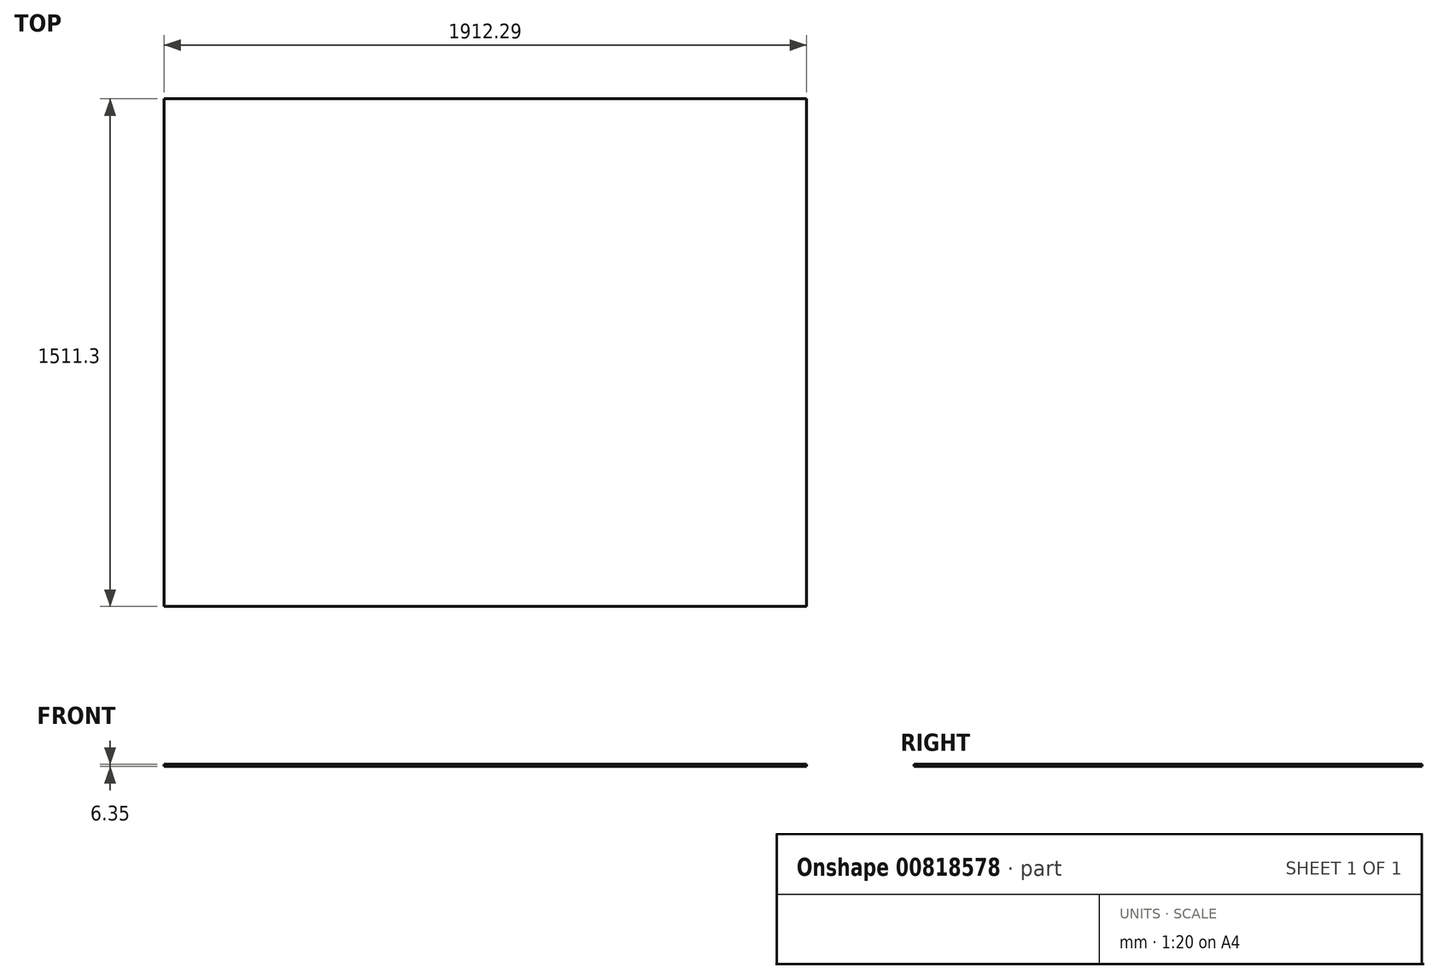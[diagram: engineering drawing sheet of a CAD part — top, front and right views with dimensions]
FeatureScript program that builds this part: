
annotation { "Feature Type Name" : "Feature", "Feature Type Description" : "" }
export const myFeature = defineFeature(function(context is Context, id is Id, definition is map)
    precondition{}
    {
        {
            var Q0;
            Q0=qCreatedBy(makeId("Top.planeOp"),FACE);
            var sketch = newSketch(context, id + "F0", { "sketchPlane" : qUnion([Q0])});
            skLineSegment(sketch, "E0.bottom", {"start": v(-953.4, 944.04) * mm, "end": v(958.9, 944.04) * mm});
            skLineSegment(sketch, "E0.top", {"start": v(-953.4, -567.26) * mm, "end": v(958.9, -567.26) * mm});
            skLineSegment(sketch, "E0.left", {"start": v(-953.4, 944.04) * mm, "end": v(-953.4, -567.26) * mm});
            skLineSegment(sketch, "E0.right", {"start": v(958.9, 944.04) * mm, "end": v(958.9, -567.26) * mm});
            skSolve(sketch);
        }
        {
            var Q0;
            Q0 = qSketchRegion(id + "F0", true);
            extrude(context, id + "F1", {"entities" : qUnion([Q0]), "depth" : 6.35 * mm, "offsetDistance" : 25.4 * mm});
        }
    });
